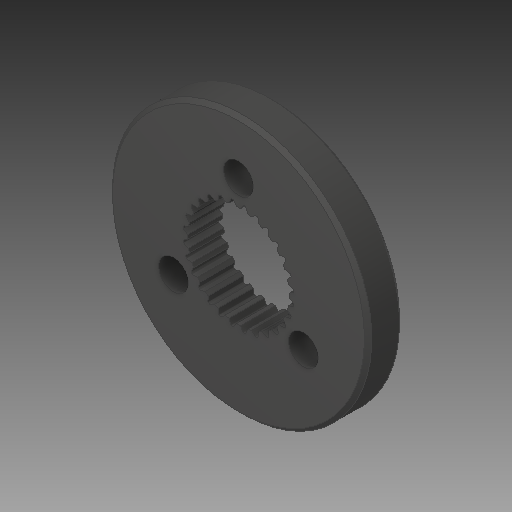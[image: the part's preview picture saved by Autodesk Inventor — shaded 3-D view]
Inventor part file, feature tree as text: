
AUTODESK INVENTOR PART (.ipt)
format: ipt  version: 2018 (Build 220112000, 112)  size: 274,944 bytes
history: native  units: in
note: dims shown in document units (in); Inventor stores cm internally (conversion verified against a paired STEP export)
features: chamfer x1
ambient origin geometry x8: Origin, YZ Plane, XZ Plane, XY Plane, X Axis, Y Axis, Z Axis, Center Point
bodies: Solid1 (feature_tree)
feature tree (1):
  chamfer  "Chamfer1"  [1 undecoded]
note: 1 required parameter value undecoded (feature->parameter linkage not recoverable at this tier; creation-order binding heuristic only, values carry confidence <= 0.55)
